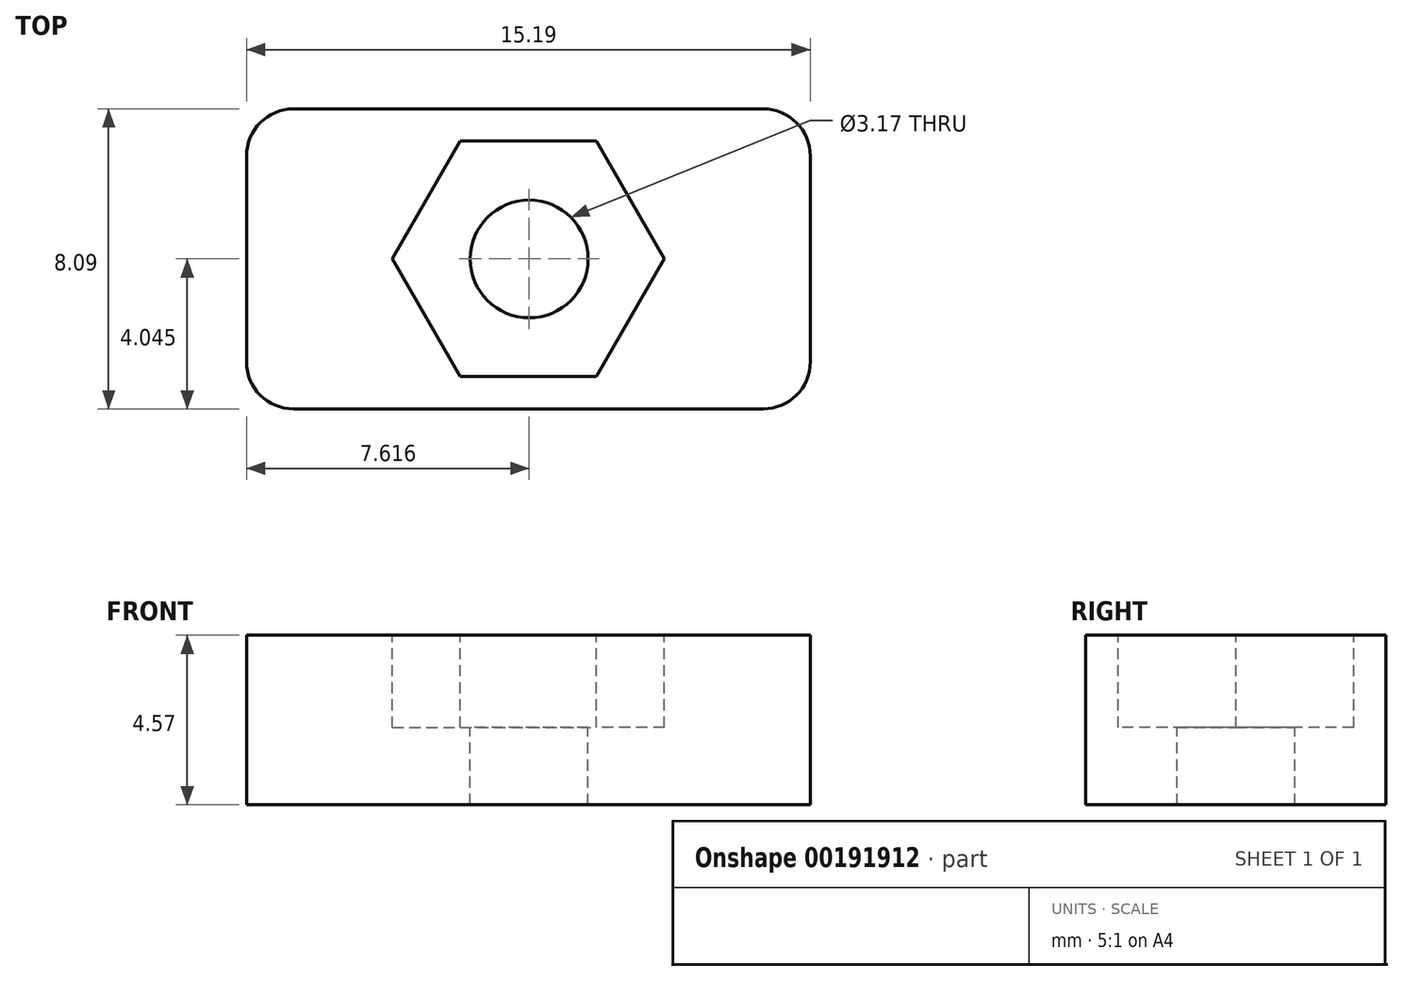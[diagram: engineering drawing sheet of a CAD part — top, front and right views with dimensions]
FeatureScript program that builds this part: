
annotation { "Feature Type Name" : "Feature", "Feature Type Description" : "" }
export const myFeature = defineFeature(function(context is Context, id is Id, definition is map)
    precondition{}
    {
        {
            var Q0;
            Q0=qCreatedBy(makeId("Top.planeOp"),FACE);
            var sketch = newSketch(context, id + "F0", { "sketchPlane" : qUnion([Q0])});
            skLineSegment(sketch, "E0.bottom", {"start": v(-11.06, 6.98) * mm, "end": v(4.13, 6.98) * mm});
            skLineSegment(sketch, "E0.top", {"start": v(-11.06, -1.1) * mm, "end": v(4.13, -1.1) * mm});
            skLineSegment(sketch, "E0.left", {"start": v(-11.06, 6.98) * mm, "end": v(-11.06, -1.1) * mm});
            skLineSegment(sketch, "E0.right", {"start": v(4.13, 6.98) * mm, "end": v(4.13, -1.1) * mm});
            skSolve(sketch);
        }
        {
            var Q0;
            Q0 = qSketchRegion(id + "F0", true);
            extrude(context, id + "F1", {"entities" : qUnion([Q0]), "depth" : 4.57 * mm});
        }
        {
            var Q0;
            Q0=makeQuery(id+"F1.opExtrude","CAP_FACE",FACE,{"disambiguationData":[OSD([sQuery(id+"F0.wireOp",EDGE,"E0.bottom"),sQuery(id+"F0.wireOp",EDGE,"E0.top"),sQuery(id+"F0.wireOp",EDGE,"E0.left"),sQuery(id+"F0.wireOp",EDGE,"E0.right")])],"isStart":false});
            var sketch = newSketch(context, id + "F2", { "sketchPlane" : qUnion([Q0])});
            skCircle(sketch, "E1.cCircle", {"center": v(-3.47, 2.94) * mm, "radius": 3.18 * mm, "construction": true});
            skLineSegment(sketch, "E1.0", {"start": v(0.2, 2.94) * mm, "end": v(-1.63, -0.24) * mm});
            skLineSegment(sketch, "E1.1", {"start": v(-1.63, -0.24) * mm, "end": v(-5.3, -0.24) * mm});
            skLineSegment(sketch, "E1.2", {"start": v(-5.3, -0.24) * mm, "end": v(-7.13, 2.94) * mm});
            skLineSegment(sketch, "E1.3", {"start": v(-7.13, 2.94) * mm, "end": v(-5.3, 6.11) * mm});
            skLineSegment(sketch, "E1.4", {"start": v(-5.3, 6.11) * mm, "end": v(-1.63, 6.11) * mm});
            skLineSegment(sketch, "E1.5", {"start": v(-1.63, 6.11) * mm, "end": v(0.2, 2.94) * mm});
            skPoint(sketch, "E1.0.midPoint", {"position": v(-0.72, 1.35) * mm});
            skSolve(sketch);
        }
        {
            var Q0;
            Q0=makeQuery(id+"F2.imprint","IMPRINT",FACE,{"disambiguationData":[TD([[makeQuery(id+"F2.imprint","IMPRINT",EDGE,{"derivedFrom":sQuery(id+"F2.wireOp",EDGE,"E1.0")}),-1.0]])]});
            extrude(context, id + "F3", {"entities" : qUnion([Q0]), "operationType" : NewBodyOperationType.REMOVE, "oppositeDirection" : true, "depth" : 2.5 * mm});
        }
        {
            var Q0;
            Q0=makeQuery(id+"F3.boolean.opBoolean","COPY",FACE,{"derivedFrom":makeQuery(id+"F3.opExtrude","CAP_FACE",FACE,{"disambiguationData":[OSD([sQuery(id+"F2.wireOp",EDGE,"E1.0"),sQuery(id+"F2.wireOp",EDGE,"E1.1"),sQuery(id+"F2.wireOp",EDGE,"E1.2"),sQuery(id+"F2.wireOp",EDGE,"E1.3"),sQuery(id+"F2.wireOp",EDGE,"E1.4"),sQuery(id+"F2.wireOp",EDGE,"E1.5")])],"isStart":false})});
            var sketch = newSketch(context, id + "F4", { "sketchPlane" : qUnion([Q0])});
            skCircle(sketch, "E2", {"center": v(-3.44, 2.94) * mm, "radius": 1.59 * mm});
            skSolve(sketch);
        }
        {
            var Q0;
            Q0 = qSketchRegion(id + "F4", true);
            extrude(context, id + "F5", {"entities" : qUnion([Q0]), "operationType" : NewBodyOperationType.REMOVE, "oppositeDirection" : true, "depth" : 25.4 * mm});
        }
        {
            var Q0;
            Q0=makeQuery(id+"F1.opExtrude","SWEPT_EDGE",EDGE,{"disambiguationData":[OSD([sQuery(id+"F0.wireOp",EDGE,"E0.top"),sQuery(id+"F0.wireOp",EDGE,"E0.right")])]});
            var Q1;
            Q1=makeQuery(id+"F1.opExtrude","SWEPT_EDGE",EDGE,{"disambiguationData":[OSD([sQuery(id+"F0.wireOp",EDGE,"E0.top"),sQuery(id+"F0.wireOp",EDGE,"E0.left")])]});
            var Q2;
            Q2=makeQuery(id+"F1.opExtrude","SWEPT_EDGE",EDGE,{"disambiguationData":[OSD([sQuery(id+"F0.wireOp",EDGE,"E0.bottom"),sQuery(id+"F0.wireOp",EDGE,"E0.left")])]});
            var Q3;
            Q3=makeQuery(id+"F1.opExtrude","SWEPT_EDGE",EDGE,{"disambiguationData":[OSD([sQuery(id+"F0.wireOp",EDGE,"E0.bottom"),sQuery(id+"F0.wireOp",EDGE,"E0.right")])]});
            fillet(context, id + "F6", {"entities" : qUnion([Q0, Q1, Q2, Q3]), "radius" : 1.27 * mm, "tangentPropagation" : true, "allowEdgeOverflow" : false});
        }
    });
